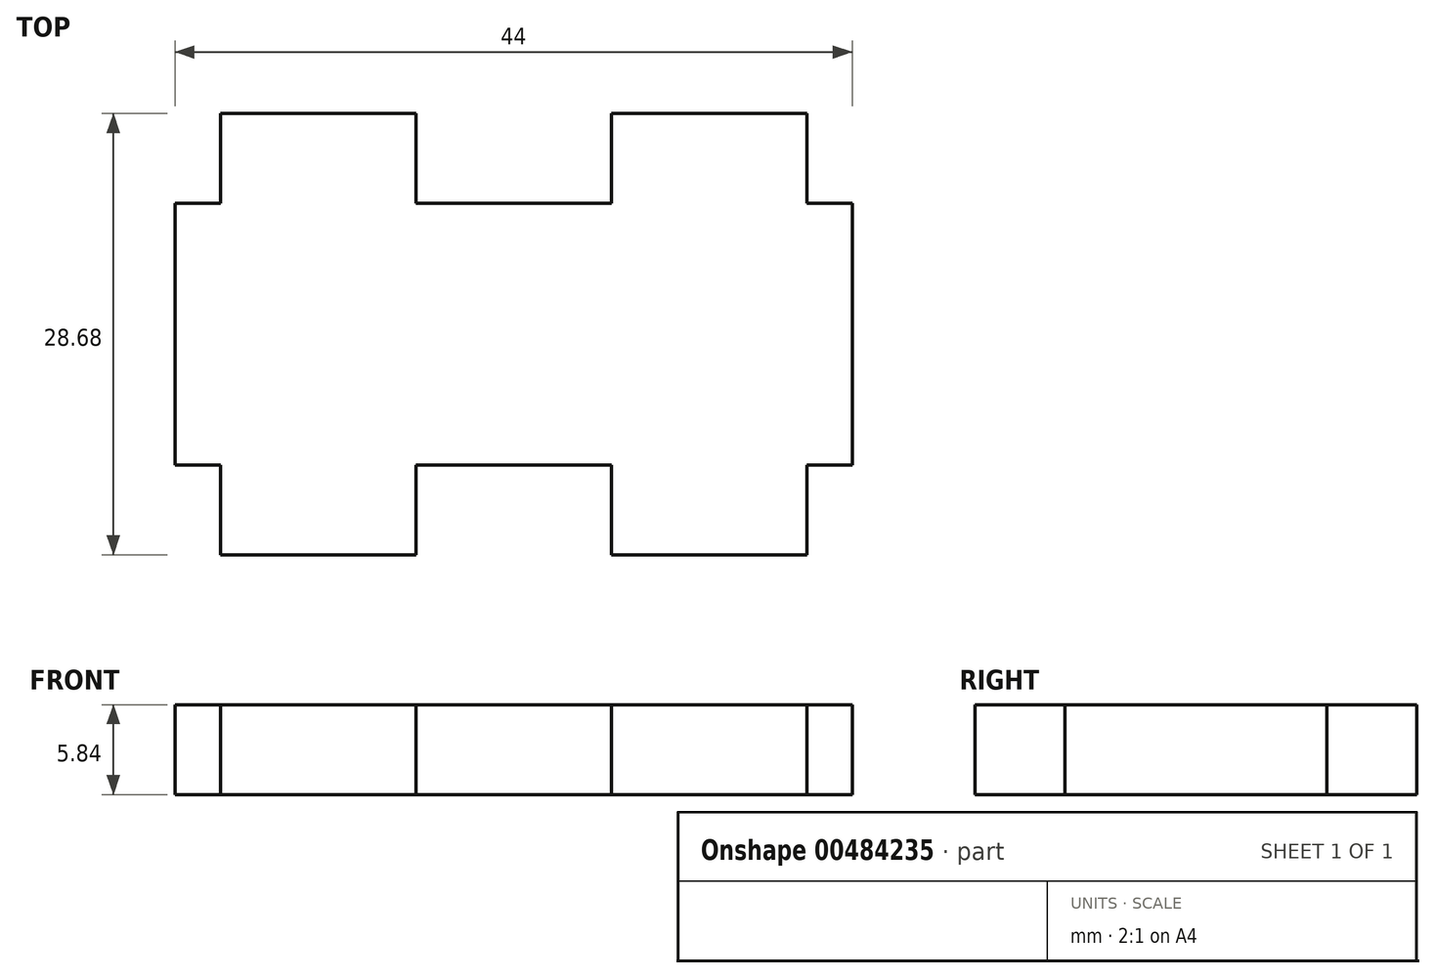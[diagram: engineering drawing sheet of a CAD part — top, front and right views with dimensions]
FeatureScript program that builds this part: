
annotation { "Feature Type Name" : "Feature", "Feature Type Description" : "" }
export const myFeature = defineFeature(function(context is Context, id is Id, definition is map)
    precondition{}
    {
        {
            var Q0;
            Q0=qCreatedBy(makeId("Top.planeOp"),FACE);
            var sketch = newSketch(context, id + "F0", { "sketchPlane" : qUnion([Q0])});
            skLineSegment(sketch, "E0.bottom", {"start": v(-22, 8.5) * mm, "end": v(-19.05, 8.5) * mm});
            skLineSegment(sketch, "E0.left", {"start": v(-22, 8.5) * mm, "end": v(-22, -8.5) * mm});
            skLineSegment(sketch, "E0.right", {"start": v(22, 8.5) * mm, "end": v(22, -8.5) * mm});
            skPoint(sketch, "E0.middle", {"position": v(0, 0) * mm});
            skLineSegment(sketch, "E1", {"start": v(0, 8.5) * mm, "end": v(0, -8.5) * mm, "construction": true});
            skLineSegment(sketch, "E2.top", {"start": v(-19.05, 14.34) * mm, "end": v(-6.35, 14.34) * mm});
            skLineSegment(sketch, "E2.left", {"start": v(-19.05, 8.5) * mm, "end": v(-19.05, 14.34) * mm});
            skLineSegment(sketch, "E2.right", {"start": v(-6.35, 8.5) * mm, "end": v(-6.35, 14.34) * mm});
            skPoint(sketch, "E2.middle", {"position": v(-12.7, 11.42) * mm});
            skLineSegment(sketch, "E3", {"start": v(-22, 0) * mm, "end": v(22, 0) * mm, "construction": true});
            skLineSegment(sketch, "E4.MirrorCS", {"start": v(6.35, 8.5) * mm, "end": v(6.35, 14.34) * mm});
            skLineSegment(sketch, "E5.MirrorCS", {"start": v(19.05, 14.34) * mm, "end": v(6.35, 14.34) * mm});
            skLineSegment(sketch, "E6.MirrorCS", {"start": v(19.05, 8.5) * mm, "end": v(19.05, 14.34) * mm});
            skPoint(sketch, "E7.MirrorP", {"position": v(-12.7, -11.42) * mm});
            skLineSegment(sketch, "E8.MirrorCS", {"start": v(19.05, -14.34) * mm, "end": v(6.35, -14.34) * mm});
            skLineSegment(sketch, "E9.MirrorCS", {"start": v(-19.05, -14.34) * mm, "end": v(-6.35, -14.34) * mm});
            skLineSegment(sketch, "E10.MirrorCS", {"start": v(19.05, -8.5) * mm, "end": v(19.05, -14.34) * mm});
            skLineSegment(sketch, "E11.MirrorCS", {"start": v(6.35, -8.5) * mm, "end": v(6.35, -14.34) * mm});
            skLineSegment(sketch, "E12.MirrorCS", {"start": v(-6.35, -8.5) * mm, "end": v(-6.35, -14.34) * mm});
            skLineSegment(sketch, "E13.MirrorCS", {"start": v(-19.05, -8.5) * mm, "end": v(-19.05, -14.34) * mm});
            skLineSegment(sketch, "E14.trimOffspring", {"start": v(-6.35, 8.5) * mm, "end": v(0, 8.5) * mm});
            skLineSegment(sketch, "E15.trimOffspring", {"start": v(19.05, 8.5) * mm, "end": v(22, 8.5) * mm});
            skLineSegment(sketch, "E16.trimOffspring", {"start": v(19.05, -8.5) * mm, "end": v(22, -8.5) * mm});
            skLineSegment(sketch, "E17.trimOffspring", {"start": v(-6.35, -8.5) * mm, "end": v(6.35, -8.5) * mm});
            skLineSegment(sketch, "E18", {"start": v(0, 8.5) * mm, "end": v(6.35, 8.5) * mm});
            skLineSegment(sketch, "E19", {"start": v(-19.05, -8.5) * mm, "end": v(-22, -8.5) * mm});
            skSolve(sketch);
        }
        {
            var Q0;
            Q0 = qSketchRegion(id + "F0", true);
            extrude(context, id + "F1", {"entities" : qUnion([Q0]), "depth" : 5.84 * mm});
        }
    });
